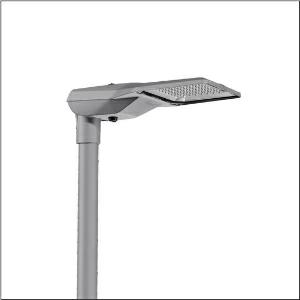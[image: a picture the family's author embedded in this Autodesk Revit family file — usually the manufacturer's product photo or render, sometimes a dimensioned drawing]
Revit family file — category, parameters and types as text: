
# Revit family: streetlight_sl_21_midi___st0_8a_5xe3c43t08lb_a4d4
name_source: partatom
category: Lighting Fixtures
units: mm (PartAtom-declared; Revit-internal decimal feet)

## family parameters
Cut with Voids When Loaded = No
Host = Face
Light Source = No
Part Type = Normal
Room Calculation Point = No
Round Connector Dimension = Use Diameter
Shared = No

## types (1)
- --- (1 x LED, 14950 lm, 98.3 W, 4000K)
    Apparent Load = 98 VA
    CIE Flux Codes = 38 75 97 100 100
    Color Rendering = 70
    Color Temperature = 4000K
    Default Elevation = 1800 mm
    Description = Streetlight SL 21 midi, mast luminaire, primary light control with lens, of PMMA, primary optical cover: cover, of toughened safety glass, transparent, light distribution: ST0.8a, light emission: direct distribution, primary light characteristic: asymmetric, installation type: side-entry, post-top, LED, High Power LED, rated luminous flux: 14.950lm, luminous efficacy: 152lm/W, light colour: 740, colour temperature: 4000K, control: overheat protection, constant luminous flux control, time-dependent luminous flux control, flexible luminous flux parameterisation, presetting dimming logarithmic, mains connection: 230..240V, AC, 50/60Hz, start of lifetime: 98W, end of service life: 101W, reduction: 45W, luminaire housing, of diecast aluminium, powder-coated, Siteco® metallic grey (DB 702S), corrosivity category C5 mid according to DIN EN ISO 12944, please order mast flange separately, inclination adjustable: 0°, 5°, 10°, 15°, sealing non-destructively replaceable, multi-level sealing system, length: 644mm, width: 335mm, height: 110mm, mast flange for spigot size: 42mm (side-entry): 5XC10008XM4, 60/48mm (side-entry/post-top): 5XC10108XM2, 76/60mm (side-entry/post-top): 5XC10108XM1, Smart Interface below and above, protection rating (complete): IP66, insulation class (complete): insulation class II (safety insulation), certification: CE, ENEC, ENEC+, VDE, impact resistance: IK09, permissible operating ambient temperature for outdoor applications: -40..+50°C, standard-compliant lighting for roads and squares, packaging unit: 1 piece

Light Distribution: ST0.8a
    Height = 111 mm
    Lamp = 1 x LED
    Lamp Light Flux = 14950 lm
    Lamp Power = 98.3 W
    Lamp count = 1
    Length = 644 mm
    Luminous efficacy = 152 lm/W
    Manufacturer = Siteco
    ModVariant = No
    Model = 5XE3C43T08LB
    Number of Poles = 1
    OnlyDefault = Yes
    Power Factor = 1
    Product Name = Streetlight SL 21 midi | ST0.8a
    Product group = mast luminaire | pylon top
    ProductGroupID = 6100
    Protection Class = Protection class II
    Protection Degree = IP 66
    RLX_Detail_Level = 1
    RLX_Emergency_Light_Flux = 0 lm
    RLX_Emergency_Type = 0
    RLX_Emergency_Type_DB = No
    RlxData = <blob elided: 91261 chars, md5=59c537a3>
    Socket = socket
    Standby Power = 0 W
    System Light Flux = 14950 lm
    System Power = 98 W
    Type Comments = factory setting: luminous flux: 100 % | dim-lin: 254 | 1020 mA
    Type Image = l_1004304.jpg
    URL = http://relux.com
    VarID = @adj_119375
    Voltage = 0 V
    Weight = 0.00 kg
    Width = 336 mm

## geometry (parser evidence)
native form markers: Blend x4, Sweep x11
no freeform markers — native parametric forms only
